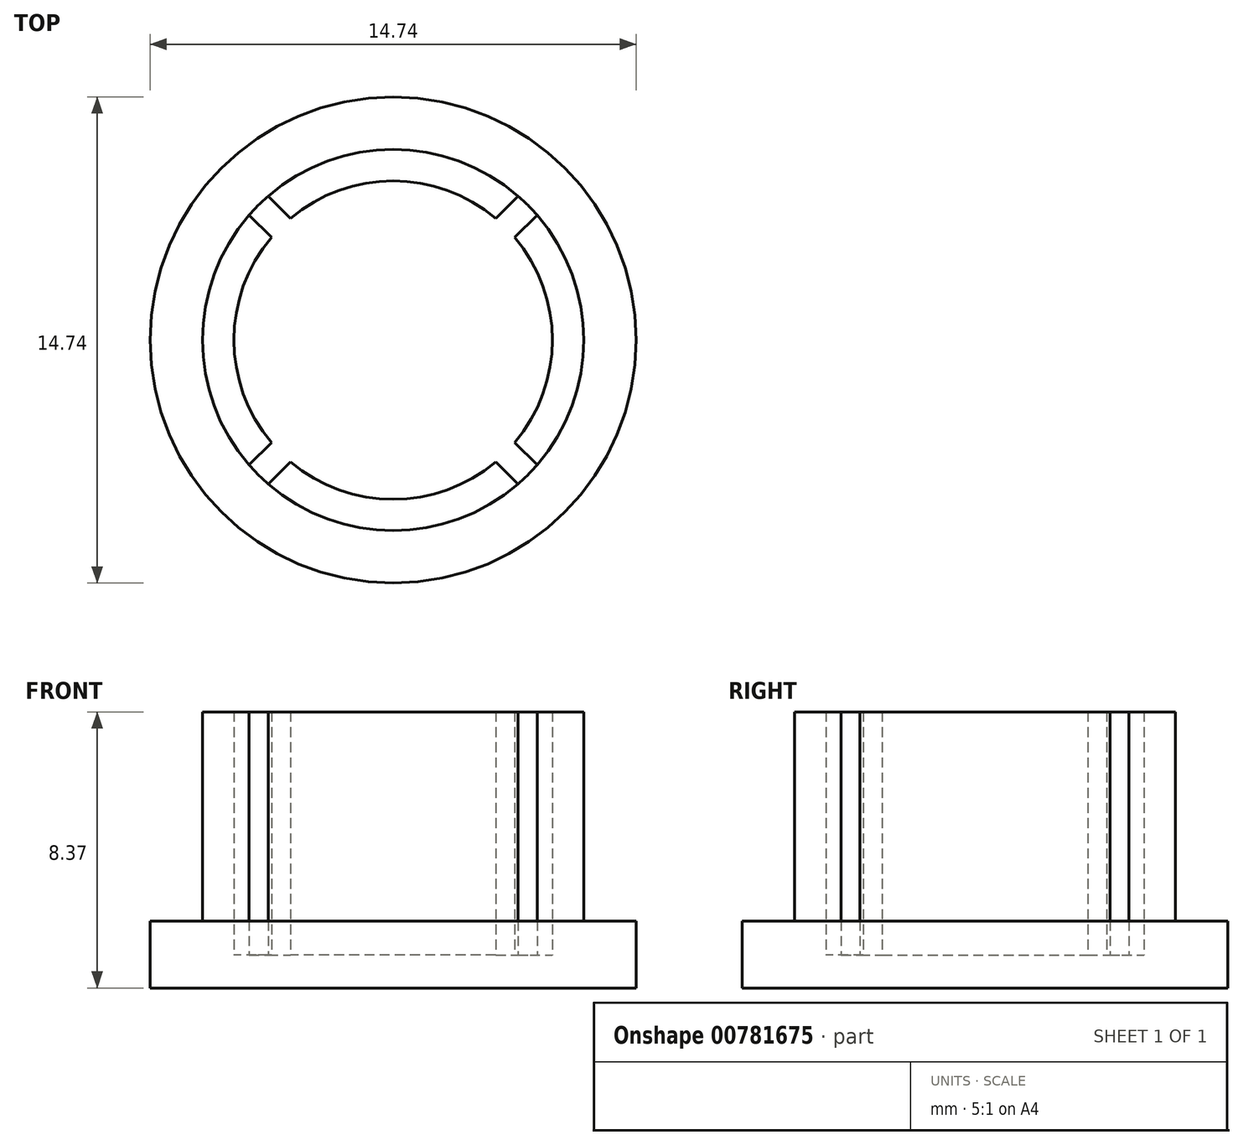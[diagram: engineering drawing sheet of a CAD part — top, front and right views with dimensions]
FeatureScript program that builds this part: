
annotation { "Feature Type Name" : "Feature", "Feature Type Description" : "" }
export const myFeature = defineFeature(function(context is Context, id is Id, definition is map)
    precondition{}
    {
        {
            var Q0;
            Q0=qCreatedBy(makeId("Top.planeOp"),FACE);
            var sketch = newSketch(context, id + "F0", { "sketchPlane" : qUnion([Q0])});
            skCircle(sketch, "E0", {"center": v(0, 0) * mm, "radius": 7.37 * mm});
            skCircle(sketch, "E1", {"center": v(0, 0) * mm, "radius": 5.78 * mm});
            skSolve(sketch);
        }
        {
            var Q0;
            Q0=makeQuery(id+"F0.imprint","IMPRINT",FACE,{"disambiguationData":[TD([[makeQuery(id+"F0.imprint","IMPRINT",EDGE,{"derivedFrom":sQuery(id+"F0.wireOp",EDGE,"E0")}),1.0]])]});
            var Q1;
            Q1=makeQuery(id+"F0.imprint","IMPRINT",FACE,{"disambiguationData":[TD([[makeQuery(id+"F0.imprint","IMPRINT",EDGE,{"derivedFrom":sQuery(id+"F0.wireOp",EDGE,"E1")}),1.0]])]});
            extrude(context, id + "F1", {"entities" : qUnion([Q0, Q1]), "depth" : 1 * mm, "offsetDistance" : 25.4 * mm});
        }
        {
            var Q0;
            Q0=qSketchRegion(id+"F0",true);
            extrude(context, id + "F2", {"entities" : qUnion([Q0]), "operationType" : NewBodyOperationType.ADD, "depth" : 2.03 * mm, "offsetDistance" : 25.4 * mm});
        }
        {
            var Q0;
            Q0=makeQuery(id+"F1.opExtrude","CAP_FACE",FACE,{"disambiguationData":[OSD([sQuery(id+"F0.wireOp",EDGE,"E0")])],"isStart":false});
            var sketch = newSketch(context, id + "F3", { "sketchPlane" : qUnion([Q0])});
            skCircle(sketch, "E2", {"center": v(0, 0) * mm, "radius": 4.83 * mm});
            skCircle(sketch, "E3.0", {"center": v(0, 0) * mm, "radius": 5.78 * mm});
            skLineSegment(sketch, "E4", {"start": v(0, 5.78) * mm, "end": v(0, -5.78) * mm, "construction": true});
            skLineSegment(sketch, "E5", {"start": v(-4.09, 4.09) * mm, "end": v(4.09, -4.09) * mm, "construction": true});
            skLineSegment(sketch, "E6", {"start": v(-4.09, -4.09) * mm, "end": v(4.09, 4.09) * mm, "construction": true});
            skLineSegment(sketch, "E7.0", {"start": v(-3.8, -4.37) * mm, "end": v(4.37, 3.8) * mm});
            skLineSegment(sketch, "E8.0", {"start": v(-4.37, -3.8) * mm, "end": v(3.8, 4.37) * mm});
            skLineSegment(sketch, "E9.0", {"start": v(-4.37, 3.8) * mm, "end": v(3.8, -4.37) * mm});
            skLineSegment(sketch, "E10.0", {"start": v(-3.8, 4.37) * mm, "end": v(4.37, -3.8) * mm});
            skSolve(sketch);
        }
        {
            var Q0;
            {var subQ0=sQuery(id+"F3.wireOp",EDGE,"E8.0");var subQ1=sQuery(id+"F3.wireOp",EDGE,"E2");var subQ2=makeQuery(id+"F3.imprint","INTERSECT",VERTEX,{"disambiguationData":[OD(0.0)],"derivedFrom":[subQ1,subQ0]});Q0=makeQuery(id+"F3.imprint","IMPRINT",FACE,{"disambiguationData":[TD([[makeQuery(id+"F3.imprint","IMPRINT",EDGE,{"disambiguationData":[TD([[subQ2,-1.0]])],"derivedFrom":subQ1}),-1.0]])]});}
            var Q1;
            {var subQ0=sQuery(id+"F3.wireOp",EDGE,"E9.0");var subQ1=sQuery(id+"F3.wireOp",EDGE,"E2");var subQ2=makeQuery(id+"F3.imprint","INTERSECT",VERTEX,{"disambiguationData":[OD(0.0)],"derivedFrom":[subQ1,subQ0]});Q1=makeQuery(id+"F3.imprint","IMPRINT",FACE,{"disambiguationData":[TD([[makeQuery(id+"F3.imprint","IMPRINT",EDGE,{"disambiguationData":[TD([[subQ2,-1.0]])],"derivedFrom":subQ1}),-1.0]])]});}
            var Q2;
            {var subQ0=sQuery(id+"F3.wireOp",EDGE,"E7.0");var subQ1=sQuery(id+"F3.wireOp",EDGE,"E2");var subQ2=makeQuery(id+"F3.imprint","INTERSECT",VERTEX,{"disambiguationData":[OD(1.0)],"derivedFrom":[subQ1,subQ0]});Q2=makeQuery(id+"F3.imprint","IMPRINT",FACE,{"disambiguationData":[TD([[makeQuery(id+"F3.imprint","IMPRINT",EDGE,{"disambiguationData":[TD([[subQ2,-1.0]])],"derivedFrom":subQ1}),-1.0]])]});}
            var Q3;
            {var subQ0=sQuery(id+"F3.wireOp",EDGE,"E7.0");var subQ1=sQuery(id+"F3.wireOp",EDGE,"E2");var subQ2=makeQuery(id+"F3.imprint","INTERSECT",VERTEX,{"disambiguationData":[OD(0.0)],"derivedFrom":[subQ1,subQ0]});Q3=makeQuery(id+"F3.imprint","IMPRINT",FACE,{"disambiguationData":[TD([[makeQuery(id+"F3.imprint","IMPRINT",EDGE,{"disambiguationData":[TD([[subQ2,1.0]])],"derivedFrom":subQ1}),-1.0]])]});}
            extrude(context, id + "F4", {"entities" : qUnion([Q0, Q1, Q2, Q3]), "operationType" : NewBodyOperationType.ADD, "depth" : 7.37 * mm, "offsetDistance" : 25.4 * mm});
        }
    });
